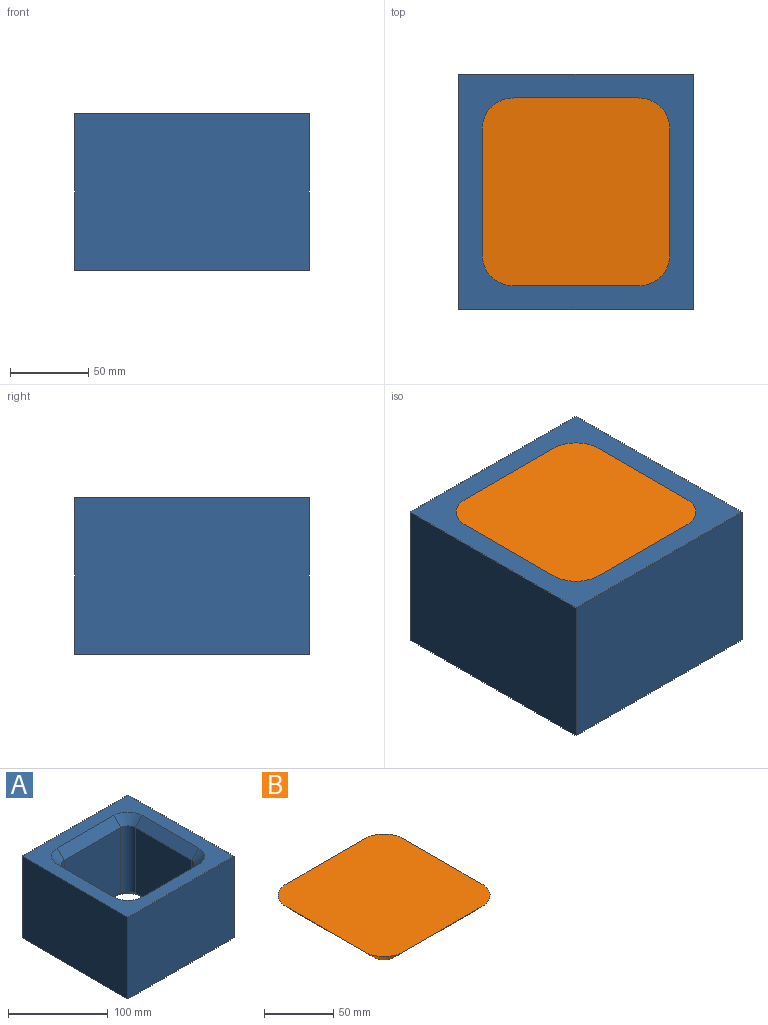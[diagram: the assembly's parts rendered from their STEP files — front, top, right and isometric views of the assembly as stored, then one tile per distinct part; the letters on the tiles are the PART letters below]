
ASSEMBLY  parts=2 mates=1
PART A: 30 faces, bbox 150x150x100 mm
  f0: plane 150x100mm, normal (1,0,0), area 15000mm2, adj f1,f11,f12,f13
  f1: plane 150x100mm, normal (0,1,0), area 15000mm2, adj f0,f2,f12,f13
  f2: plane 150x100mm, normal (-1,0,0), area 15000mm2, adj f1,f11,f12,f13
  f3: plane 80x80mm, normal (0,-1,0), area 6400mm2, adj f4,f10,f18,f26
  f4: cylinder r=10mm len=80mm, axis (0,0,1), area 1256.6mm2, adj f3,f5,f20,f24
  f5: plane 80x80mm, normal (-1,0,0), area 6400mm2, adj f4,f6,f21,f22
  f6: cylinder r=10mm len=80mm, axis (0,0,1), area 1256.6mm2, adj f5,f7,f19,f23
  f7: plane 80x80mm, normal (0,1,0), area 6400mm2, adj f6,f8,f17,f25
  f8: cylinder r=10mm len=80mm, axis (0,0,1), area 1256.6mm2, adj f7,f9,f15,f27
  f9: plane 80x80mm, normal (1,0,0), area 6400mm2, adj f8,f10,f14,f29
  f10: cylinder r=10mm len=80mm, axis (0,0,1), area 1256.6mm2, adj f3,f9,f16,f28
  f11: plane 150x100mm, normal (0,-1,0), area 15000mm2, adj f0,f2,f12,f13
  f12: plane 150x150mm, normal (0,0,-1), area 8443.4mm2, adj f0,f1,f2,f11,f22,f23,f24,f25
  f13: plane 150x150mm, normal (0,0,1), area 8443.4mm2, adj f0,f1,f2,f11,f14,f15,f16,f17
  f14: plane 80x10mm, normal (0.71,0,0.71), area 1131.4mm2, adj f9,f13,f15,f16
  f15: cone r=10mm half-angle=45deg, axis (0,0,1), area 333.2mm2, adj f8,f13,f14,f17
  f16: cone r=10mm half-angle=45deg, axis (0,0,1), area 333.2mm2, adj f10,f13,f14,f18
  f17: plane 80x10mm, normal (0,0.71,0.71), area 1131.4mm2, adj f7,f13,f15,f19
  f18: plane 80x10mm, normal (0,-0.71,0.71), area 1131.4mm2, adj f3,f13,f16,f20
  f19: cone r=10mm half-angle=45deg, axis (0,0,1), area 333.2mm2, adj f6,f13,f17,f21
  f20: cone r=10mm half-angle=45deg, axis (0,0,1), area 333.2mm2, adj f4,f13,f18,f21
  f21: plane 80x10mm, normal (-0.71,0,0.71), area 1131.4mm2, adj f5,f13,f19,f20
  f22: plane 80x10mm, normal (-0.71,0,-0.71), area 1131.4mm2, adj f5,f12,f23,f24
  f23: cone r=20mm half-angle=45deg, axis (0,0,-1), area 333.2mm2, adj f6,f12,f22,f25
  f24: cone r=20mm half-angle=45deg, axis (0,0,-1), area 333.2mm2, adj f4,f12,f22,f26
  f25: plane 80x10mm, normal (0,0.71,-0.71), area 1131.4mm2, adj f7,f12,f23,f27
  f26: plane 80x10mm, normal (0,-0.71,-0.71), area 1131.4mm2, adj f3,f12,f24,f28
  f27: cone r=20mm half-angle=45deg, axis (0,0,-1), area 333.2mm2, adj f8,f12,f25,f29
  f28: cone r=20mm half-angle=45deg, axis (0,0,-1), area 333.2mm2, adj f10,f12,f26,f29
  f29: plane 80x10mm, normal (0.71,0,-0.71), area 1131.4mm2, adj f9,f12,f27,f28
PART B: 10 faces, bbox 120x120x10 mm
  f0: plane 120x120mm, normal (0,0,1), area 14056.6mm2, adj f2,f3,f4,f5,f6,f7,f8,f9
  f1: plane 100x100mm, normal (0,0,-1), area 9914.2mm2, adj f2,f3,f4,f5,f6,f7,f8,f9
  f2: plane 80x10mm, normal (-0.71,0,-0.71), area 1131.4mm2, adj f0,f1,f3,f4
  f3: cone r=20mm half-angle=45deg, axis (0,0,1), area 333.2mm2, adj f0,f1,f2,f5
  f4: cone r=20mm half-angle=45deg, axis (0,0,1), area 333.2mm2, adj f0,f1,f2,f6
  f5: plane 80x10mm, normal (0,-0.71,-0.71), area 1131.4mm2, adj f0,f1,f3,f7
  f6: plane 80x10mm, normal (0,0.71,-0.71), area 1131.4mm2, adj f0,f1,f4,f8
  f7: cone r=20mm half-angle=45deg, axis (0,0,1), area 333.2mm2, adj f0,f1,f5,f9
  f8: cone r=20mm half-angle=45deg, axis (0,0,1), area 333.2mm2, adj f0,f1,f6,f9
  f9: plane 80x10mm, normal (0.71,0,-0.71), area 1131.4mm2, adj f0,f1,f7,f8
PLACE A t=(-45.66,-28.3,28.81)mm
PLACE B t=(-45.66,-28.3,18.81)mm
MATE fastened B.f5 <-> A.f17  axis (0,-0.71,-0.71) through (-45.66,-88.3,28.81)mm
